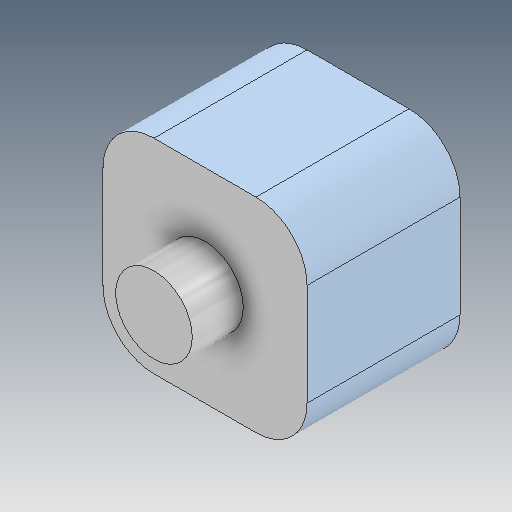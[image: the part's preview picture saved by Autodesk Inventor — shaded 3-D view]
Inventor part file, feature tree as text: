
AUTODESK INVENTOR PART (.ipt)
format: ipt  version: 2021 (Build 250183000, 183)  size: 127,488 bytes
history: native  units: mm
features: extrude x2, sketch x2, fillet x1
ambient origin geometry x8: Origin, YZ Plane, XZ Plane, XY Plane, X Axis, Y Axis, Z Axis, Center Point
bodies: Solid1 (feature_tree)
feature tree (5):
  extrude  "Extrusion1"  Depth=10.0mm TaperAngle=0.0deg
  extrude  "Extrusion2"  Depth=40.0mm
  fillet  "Fillet1"  Radius=30.0mm
  sketch  "Sketch1"  dims[d0=15.0mm d1=10.0mm d2=0.0mm]
  sketch  "Sketch2"  dims[d3=40.0mm d4=40.0mm d5=30.0mm d6=0.0mm d7=10.0mm]
